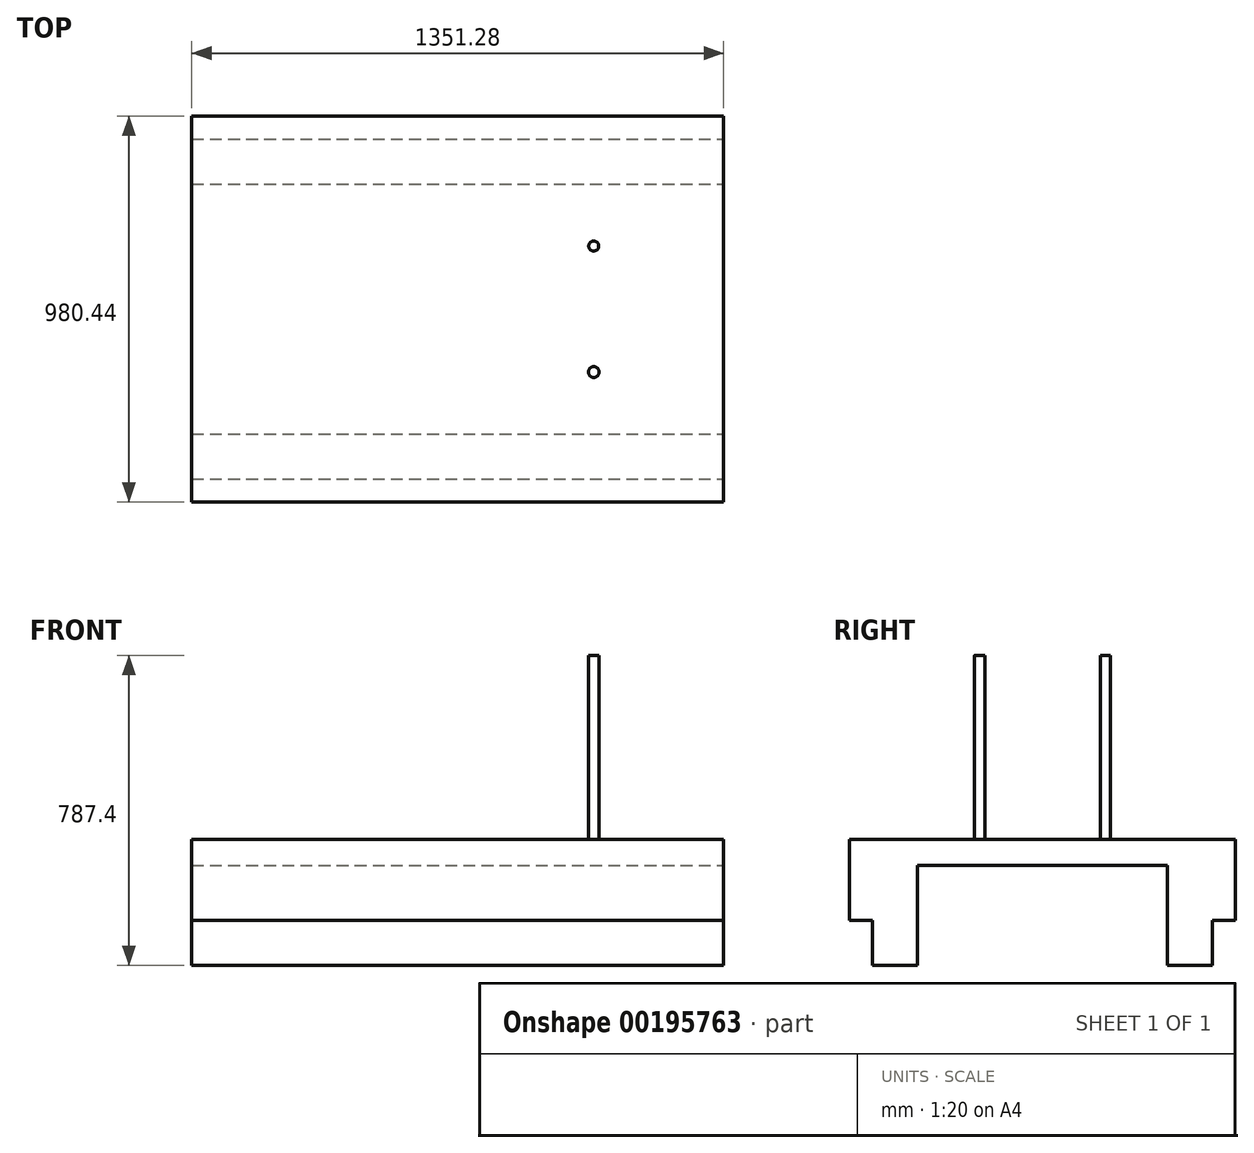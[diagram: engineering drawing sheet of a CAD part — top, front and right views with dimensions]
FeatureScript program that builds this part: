
annotation { "Feature Type Name" : "Feature", "Feature Type Description" : "" }
export const myFeature = defineFeature(function(context is Context, id is Id, definition is map)
    precondition{}
    {
        {
            var Q0;
            Q0=qCreatedBy(makeId("Top.planeOp"),FACE);
            var sketch = newSketch(context, id + "F0", { "sketchPlane" : qUnion([Q0])});
            skLineSegment(sketch, "E0.bottom", {"start": v(-927.02, 0) * mm, "end": v(424.26, 0) * mm});
            skLineSegment(sketch, "E0.top", {"start": v(-927.02, 980.44) * mm, "end": v(424.26, 980.44) * mm});
            skLineSegment(sketch, "E0.left", {"start": v(-927.02, 0) * mm, "end": v(-927.02, 980.44) * mm});
            skLineSegment(sketch, "E0.right", {"start": v(424.26, 0) * mm, "end": v(424.26, 980.44) * mm});
            skSolve(sketch);
        }
        {
            var Q0;
            Q0=makeQuery(id+"F0.imprint","IMPRINT",FACE,{"disambiguationData":[TD([[makeQuery(id+"F0.imprint","IMPRINT",EDGE,{"derivedFrom":sQuery(id+"F0.wireOp",EDGE,"E0.bottom")}),1.0]])]});
            extrude(context, id + "F1", {"entities" : qUnion([Q0]), "depth" : 320.04 * mm});
        }
        {
            var Q0;
            Q0=makeQuery(id+"F1.opExtrude","CAP_FACE",FACE,{"disambiguationData":[OSD([sQuery(id+"F0.wireOp",EDGE,"E0.bottom"),sQuery(id+"F0.wireOp",EDGE,"E0.top"),sQuery(id+"F0.wireOp",EDGE,"E0.left"),sQuery(id+"F0.wireOp",EDGE,"E0.right")])],"isStart":false});
            var sketch = newSketch(context, id + "F2", { "sketchPlane" : qUnion([Q0])});
            skCircle(sketch, "E1", {"center": v(94.06, 650.24) * mm, "radius": 12.7 * mm});
            skCircle(sketch, "E2", {"center": v(94.06, 330.2) * mm, "radius": 13.64 * mm});
            skSolve(sketch);
        }
        {
            var Q0;
            Q0 = qSketchRegion(id + "F2", true);
            extrude(context, id + "F3", {"entities" : qUnion([Q0]), "operationType" : NewBodyOperationType.ADD, "depth" : 467.36 * mm});
        }
        {
            var Q0;
            Q0=makeQuery(id+"F1.opExtrude","SWEPT_FACE",FACE,{"disambiguationData":[OSD([sQuery(id+"F0.wireOp",EDGE,"E0.right")])]});
            var sketch = newSketch(context, id + "F4", { "sketchPlane" : qUnion([Q0])});
            skLineSegment(sketch, "E3", {"start": v(490.22, 320.04) * mm, "end": v(490.22, 0) * mm, "construction": true});
            skLineSegment(sketch, "E4", {"start": v(490.22, 254) * mm, "end": v(172.72, 254) * mm});
            skLineSegment(sketch, "E5", {"start": v(172.72, 254) * mm, "end": v(172.72, 0) * mm});
            skLineSegment(sketch, "E6", {"start": v(172.72, 0) * mm, "end": v(490.22, 0) * mm});
            skLineSegment(sketch, "E7.MirrorCS", {"start": v(490.22, 254) * mm, "end": v(807.72, 254) * mm});
            skLineSegment(sketch, "E8.MirrorCS", {"start": v(807.72, 254) * mm, "end": v(807.72, 0) * mm});
            skLineSegment(sketch, "E9.MirrorCS", {"start": v(807.72, 0) * mm, "end": v(490.22, 0) * mm});
            skSolve(sketch);
        }
        {
            var Q0;
            Q0=makeQuery(id+"F4.imprint","IMPRINT",FACE,{"disambiguationData":[TD([[makeQuery(id+"F4.imprint","IMPRINT",EDGE,{"derivedFrom":sQuery(id+"F4.wireOp",EDGE,"E4")}),1.0]])]});
            extrude(context, id + "F5", {"entities" : qUnion([Q0]), "operationType" : NewBodyOperationType.REMOVE, "oppositeDirection" : true, "depth" : 1351.28 * mm});
        }
        {
            var Q0;
            Q0=makeQuery(id+"F1.opExtrude","SWEPT_FACE",FACE,{"disambiguationData":[OSD([sQuery(id+"F0.wireOp",EDGE,"E0.right")])]});
            var sketch = newSketch(context, id + "F6", { "sketchPlane" : qUnion([Q0])});
            skLineSegment(sketch, "E10.bottom", {"start": v(0, 0) * mm, "end": v(58.42, 0) * mm});
            skLineSegment(sketch, "E10.top", {"start": v(0, 114.73) * mm, "end": v(58.42, 114.73) * mm});
            skLineSegment(sketch, "E10.left", {"start": v(0, 0) * mm, "end": v(0, 114.73) * mm});
            skLineSegment(sketch, "E10.right", {"start": v(58.42, 0) * mm, "end": v(58.42, 114.73) * mm});
            skLineSegment(sketch, "E11", {"start": v(490.22, 320.04) * mm, "end": v(490.22, 0) * mm, "construction": true});
            skLineSegment(sketch, "E12.MirrorCS", {"start": v(922.02, 0) * mm, "end": v(922.02, 114.73) * mm});
            skLineSegment(sketch, "E13.MirrorCS", {"start": v(980.44, 114.73) * mm, "end": v(922.02, 114.73) * mm});
            skLineSegment(sketch, "E14.MirrorCS", {"start": v(980.44, 0) * mm, "end": v(980.44, 114.73) * mm});
            skLineSegment(sketch, "E15.MirrorCS", {"start": v(980.44, 0) * mm, "end": v(922.02, 0) * mm});
            skSolve(sketch);
        }
        {
            var Q0;
            Q0=makeQuery(id+"F6.imprint","IMPRINT",FACE,{"disambiguationData":[TD([[makeQuery(id+"F6.imprint","IMPRINT",EDGE,{"derivedFrom":sQuery(id+"F6.wireOp",EDGE,"E10.bottom")}),1.0]])]});
            var Q1;
            Q1=makeQuery(id+"F6.imprint","IMPRINT",FACE,{"disambiguationData":[TD([[makeQuery(id+"F6.imprint","IMPRINT",EDGE,{"derivedFrom":sQuery(id+"F6.wireOp",EDGE,"E12.MirrorCS")}),-1.0]])]});
            extrude(context, id + "F7", {"entities" : qUnion([Q0, Q1]), "operationType" : NewBodyOperationType.REMOVE, "oppositeDirection" : true, "depth" : 1356.36 * mm});
        }
    });
